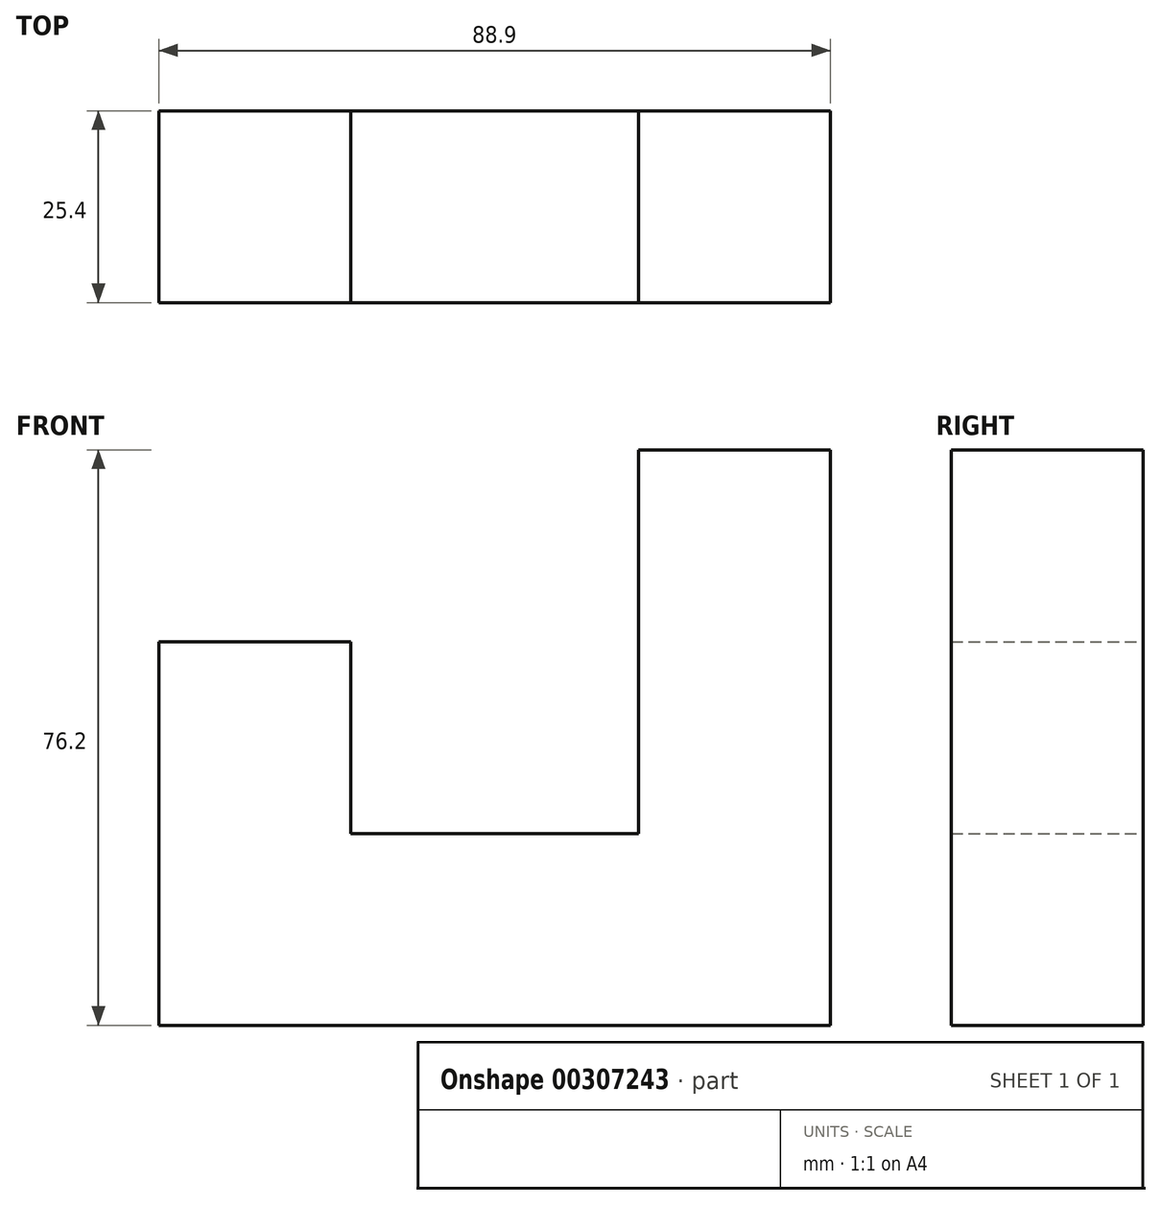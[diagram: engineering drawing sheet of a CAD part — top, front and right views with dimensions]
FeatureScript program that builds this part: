
annotation { "Feature Type Name" : "Feature", "Feature Type Description" : "" }
export const myFeature = defineFeature(function(context is Context, id is Id, definition is map)
    precondition{}
    {
        {
            var Q0;
            Q0=qCreatedBy(makeId("Front.planeOp"),FACE);
            var sketch = newSketch(context, id + "F0", { "sketchPlane" : qUnion([Q0])});
            skLineSegment(sketch, "E0", {"start": v(20.9, -9.56) * mm, "end": v(20.9, 41.24) * mm});
            skLineSegment(sketch, "E1", {"start": v(20.9, 41.24) * mm, "end": v(46.3, 41.24) * mm});
            skLineSegment(sketch, "E2", {"start": v(46.3, 41.24) * mm, "end": v(46.3, -34.96) * mm});
            skLineSegment(sketch, "E3", {"start": v(46.3, -34.96) * mm, "end": v(-42.6, -34.96) * mm});
            skLineSegment(sketch, "E4", {"start": v(-42.6, -34.96) * mm, "end": v(-42.6, 15.84) * mm});
            skLineSegment(sketch, "E5", {"start": v(-42.6, 15.84) * mm, "end": v(-17.2, 15.84) * mm});
            skLineSegment(sketch, "E6", {"start": v(-17.2, 15.84) * mm, "end": v(-17.2, -9.56) * mm});
            skLineSegment(sketch, "E7", {"start": v(-17.2, -9.56) * mm, "end": v(20.9, -9.56) * mm});
            skSolve(sketch);
        }
        {
            var Q0;
            Q0=makeQuery(id+"F0.imprint","IMPRINT",FACE,{"disambiguationData":[TD([[makeQuery(id+"F0.imprint","IMPRINT",EDGE,{"derivedFrom":sQuery(id+"F0.wireOp",EDGE,"E0")}),-1.0]])]});
            extrude(context, id + "F1", {"entities" : qUnion([Q0]), "depth" : 25.4 * mm});
        }
    });
